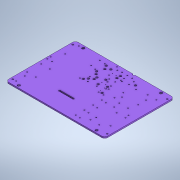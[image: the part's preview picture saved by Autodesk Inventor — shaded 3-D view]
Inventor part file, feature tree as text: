
AUTODESK INVENTOR PART (.ipt)
format: ipt  version: 2021 (Build 250183000, 183)  size: 600,576 bytes
history: native  units: mm
features: sketch x31, hole x28, projected_geometry x3, extrude x2
ambient origin geometry x8: Origin, YZ Plane, XZ Plane, XY Plane, X Axis, Y Axis, Z Axis, Center Point
bodies: Solid1 (feature_tree)
feature tree (64):
  extrude  "Extrusion1"  Depth=350.0mm
  hole  "Hole1"  [1 undecoded]
  hole  "Hole3"  [1 undecoded]
  hole  "Hole4"  [1 undecoded]
  hole  "Hole5"  [1 undecoded]
  hole  "Hole6"  [1 undecoded]
  hole  "Hole7"  [1 undecoded]
  hole  "Hole8"  [1 undecoded]
  hole  "Hole9"  [1 undecoded]
  hole  "Hole10"  [1 undecoded]
  hole  "Hole11"  [1 undecoded]
  hole  "Hole12"  [1 undecoded]
  hole  "Hole13"  [1 undecoded]
  hole  "Hole14"  [1 undecoded]
  hole  "Hole15"  [1 undecoded]
  hole  "Hole16"  [1 undecoded]
  hole  "Hole17"  [1 undecoded]
  hole  "Hole18"  [1 undecoded]
  hole  "Hole19"  [1 undecoded]
  hole  "Hole20"  [1 undecoded]
  hole  "Hole21"  [1 undecoded]
  hole  "Hole22"  [1 undecoded]
  hole  "Hole23"  [1 undecoded]
  hole  "Hole24"  [1 undecoded]
  hole  "Hole25"  [1 undecoded]
  sketch  "Sketch28"  dims[d152=7.5mm d153=6.0mm d154=4.0mm d155=2.0mm d156=90.0deg d157=8.0mm d158=20.594885mm d159=139.6mm]
  hole  "Hole27"  [1 undecoded]
  extrude  "Extrusion3"  Depth=10.0mm
  hole  "Hole28"  [1 undecoded]
  hole  "Hole29"  [1 undecoded]
  hole  "Hole30"  [1 undecoded]
  sketch  "Sketch1"  dims[d9=5.0mm d10=0.0mm d31=350.0mm]
  sketch  "Sketch2"  dims[d32=246.0mm d33=10.0mm]
  projected_geometry  "Projected Loop1"
  sketch  "Sketch5"  dims[d34=275.7mm d35=227.8mm]
  sketch  "Sketch6"  dims[d40=335.0mm d41=213.0mm]
  sketch  "Sketch7"  dims[d42=5.6mm d43=6.0mm d44=4.0mm d45=2.0mm d46=90.0deg d47=8.0mm d48=20.594885mm d72=31.0mm]
  sketch  "Sketch8"  dims[d74=3.8mm d75=6.0mm d76=4.0mm d77=2.0mm d78=90.0deg d79=8.0mm d80=20.594885mm d82=30.0mm]
  sketch  "Sketch9"  dims[d83=114.0mm d84=80.25mm]
  projected_geometry  "Projected Loop2"
  sketch  "Sketch10"  dims[d85=80.25mm d86=31.0mm]
  sketch  "Sketch11"  dims[d87=31.0mm]
  sketch  "Sketch12"  dims[d88=3.8mm d89=6.0mm d90=4.0mm d91=2.0mm d92=90.0deg d93=8.0mm d94=20.594885mm d95=31.0mm]
  sketch  "Sketch13"  dims[d96=41.75mm d97=64.0mm]
  sketch  "Sketch14"  dims[d98=50.0mm]
  sketch  "Sketch15"  dims[d99=3.8mm d100=6.0mm d101=4.0mm d102=2.0mm d103=90.0deg d104=8.0mm d105=20.594885mm d106=85.0mm]
  sketch  "Sketch16"  dims[d107=25.0mm d108=31.0mm]
  sketch  "Sketch17"  dims[d109=24.25mm d110=24.25mm]
  sketch  "Sketch18"  dims[d111=18.75mm d112=17.0mm]
  sketch  "Sketch19"  dims[d113=31.0mm]
  sketch  "Sketch20"  dims[d114=3.8mm d115=6.0mm d116=4.0mm d117=2.0mm d118=90.0deg d119=8.0mm d120=20.594885mm d121=226.0mm]
  sketch  "Sketch21"  dims[d122=17.0mm d123=31.0mm]
  sketch  "Sketch22"  dims[d124=3.8mm d125=6.0mm d126=4.0mm d127=2.0mm d128=90.0deg d129=8.0mm d130=20.594885mm d131=123.5mm]
  sketch  "Sketch23"  dims[d132=31.0mm d133=102.0mm]
  sketch  "Sketch24"  dims[d134=22.5mm d135=117.2mm]
  sketch  "Sketch25"  dims[d136=10.0mm d137=12.0mm]
  sketch  "Sketch26"  dims[d138=58.6mm d139=46.6mm]
  sketch  "Sketch27"  dims[d141=3.8mm d142=6.0mm d143=4.0mm d144=2.0mm d145=90.0deg d146=8.0mm d147=20.594885mm d148=131.65mm]
  sketch  "Sketch29"  dims[d163=7.5mm d164=6.0mm d165=4.0mm d166=2.0mm d167=90.0deg d168=8.0mm d169=20.594885mm d170=151.25mm]
  projected_geometry  "Projected Loop3"
  sketch  "Sketch30"  dims[d171=151.25mm]
  sketch  "Sketch31"  dims[d175=7.5mm d176=6.0mm d177=4.0mm d178=2.0mm d179=90.0deg d180=8.0mm d181=20.594885mm d182=22.163mm]
  sketch  "Sketch32"  dims[d184=56.3mm d185=103.2mm]
  sketch  "Sketch33"  dims[d186=35.3mm d187=66.2mm d188=93.3mm d189=25.4mm d190=74.8mm d191=84.7mm d192=174.25mm d193=66.2mm d194=93.3mm d195=7.5mm d196=6.0mm d197=4.0mm d198=2.0mm d199=90.0deg d200=8.0mm d201=20.594885mm d202=29.05mm d203=41.35mm d204=84.7mm d205=198.85mm d206=188.85mm d207=7.5mm d208=6.0mm d209=4.0mm d210=2.0mm d211=90.0deg d212=8.0mm d213=20.594885mm d214=244.203mm d215=30.76mm d216=0.229mm d217=113.039mm d218=208.1mm d219=7.5mm d220=6.0mm d221=4.0mm d222=2.0mm d223=90.0deg d224=8.0mm d225=20.594885mm d226=29.979mm d227=40.779mm d228=69.4mm d229=183.45mm d230=202.7mm d231=3.8mm d232=6.0mm d233=4.0mm d234=2.0mm d235=90.0deg d236=8.0mm d237=20.594885mm d238=197.35mm d239=94.049mm d240=107.517mm d241=1.85mm d242=6.0mm d243=4.0mm d244=2.0mm d245=90.0deg d246=8.0mm d247=20.594885mm d248=80.868mm d249=175.003mm d250=188.471mm d251=1.85mm d252=6.0mm d253=4.0mm d254=2.0mm d255=90.0deg d256=8.0mm d257=20.594885mm d258=35.161mm d259=180.073mm d260=166.605mm d261=1.85mm d262=6.0mm d263=4.0mm d264=2.0mm d265=90.0deg d266=8.0mm d267=20.594885mm d268=8.6mm d269=3.7mm d270=3.7mm d271=3.7mm d275=3.7mm d276=8.6mm d277=28.6mm d278=14.5mm d279=3.8mm d280=6.0mm d281=4.0mm d282=2.0mm d283=90.0deg d284=8.0mm d285=20.594885mm d286=14.5mm d287=14.5mm d288=8.6mm d289=20.8mm d290=18.6mm d291=3.7mm d292=3.8mm d293=6.0mm d294=4.0mm d295=2.0mm d296=90.0deg d297=8.0mm d298=20.594885mm d299=8.6mm d300=8.6mm d301=3.7mm d302=3.7mm d303=3.8mm d304=6.0mm d305=4.0mm d306=2.0mm d307=90.0deg d308=8.0mm d309=20.594885mm d310=14.5mm d311=8.6mm d312=14.5mm d313=8.6mm d314=8.6mm d315=8.6mm d316=3.7mm d317=3.7mm d318=3.7mm d319=3.7mm d320=8.6mm d321=8.6mm d322=3.8mm d323=6.0mm d324=4.0mm d325=2.0mm d326=90.0deg d327=8.0mm d328=20.594885mm d329=8.6mm d330=8.6mm d331=14.5mm d332=14.5mm d333=14.5mm d334=14.5mm d335=8.6mm d336=8.6mm d337=3.8mm d338=6.0mm d339=4.0mm d340=2.0mm d341=90.0deg d342=8.0mm d343=20.594885mm d348=208.275mm d349=208.275mm d354=43.0mm d355=90.0mm d356=3.8mm d357=6.0mm d358=4.0mm d359=2.0mm d360=90.0deg d361=8.0mm d362=20.594885mm d363=107.95mm d364=53.34mm d365=3.0mm d366=5.5mm d367=3.34mm d368=5.5mm d370=2.54mm d371=54.61mm d372=53.34mm d373=2.54mm d374=2.54mm d375=7.62mm d376=17.78mm d377=59.0mm d378=91.5mm d379=15.0mm d380=15.0mm d381=12.5mm d382=12.5mm d383=4.0mm d384=4.0mm d385=4.0mm d386=4.0mm d387=273.0mm d388=135.0mm d389=3.8mm d390=6.0mm d391=4.0mm d392=2.0mm d393=90.0deg d394=8.0mm d395=20.594885mm d396=8.4mm d397=0.6mm d398=8.4mm d399=0.6mm d400=8.4mm d401=0.6mm d402=8.4mm d403=0.6mm d404=9.1mm d405=9.1mm d406=59.5mm d407=61.25mm d415=61.75mm d416=61.75mm d417=3.8mm d418=6.0mm d419=4.0mm d420=2.0mm d421=90.0deg d422=8.0mm d423=20.594885mm d424=64.25mm d427=50.0mm d429=5.05mm d430=125.0mm d431=10.0mm d432=0.0mm d433=117.5mm d434=6.0mm d435=12.0mm d436=12.0mm d437=3.8mm d438=6.0mm d439=4.0mm d440=2.0mm d441=90.0deg d442=8.0mm d443=20.594885mm d445=18.0mm d446=48.75mm d447=79.75mm d448=110.5mm d449=3.8mm d450=6.0mm d451=4.0mm d452=2.0mm d453=90.0deg d454=8.0mm d455=20.594885mm d456=120.5mm d457=104.0mm d458=17.0mm d459=31.0mm d460=3.8mm d461=6.0mm d462=4.0mm d463=2.0mm d464=90.0deg d465=8.0mm d466=20.594885mm]
note: 28 required parameter values undecoded (feature->parameter linkage not recoverable at this tier; creation-order binding heuristic only, values carry confidence <= 0.55)
